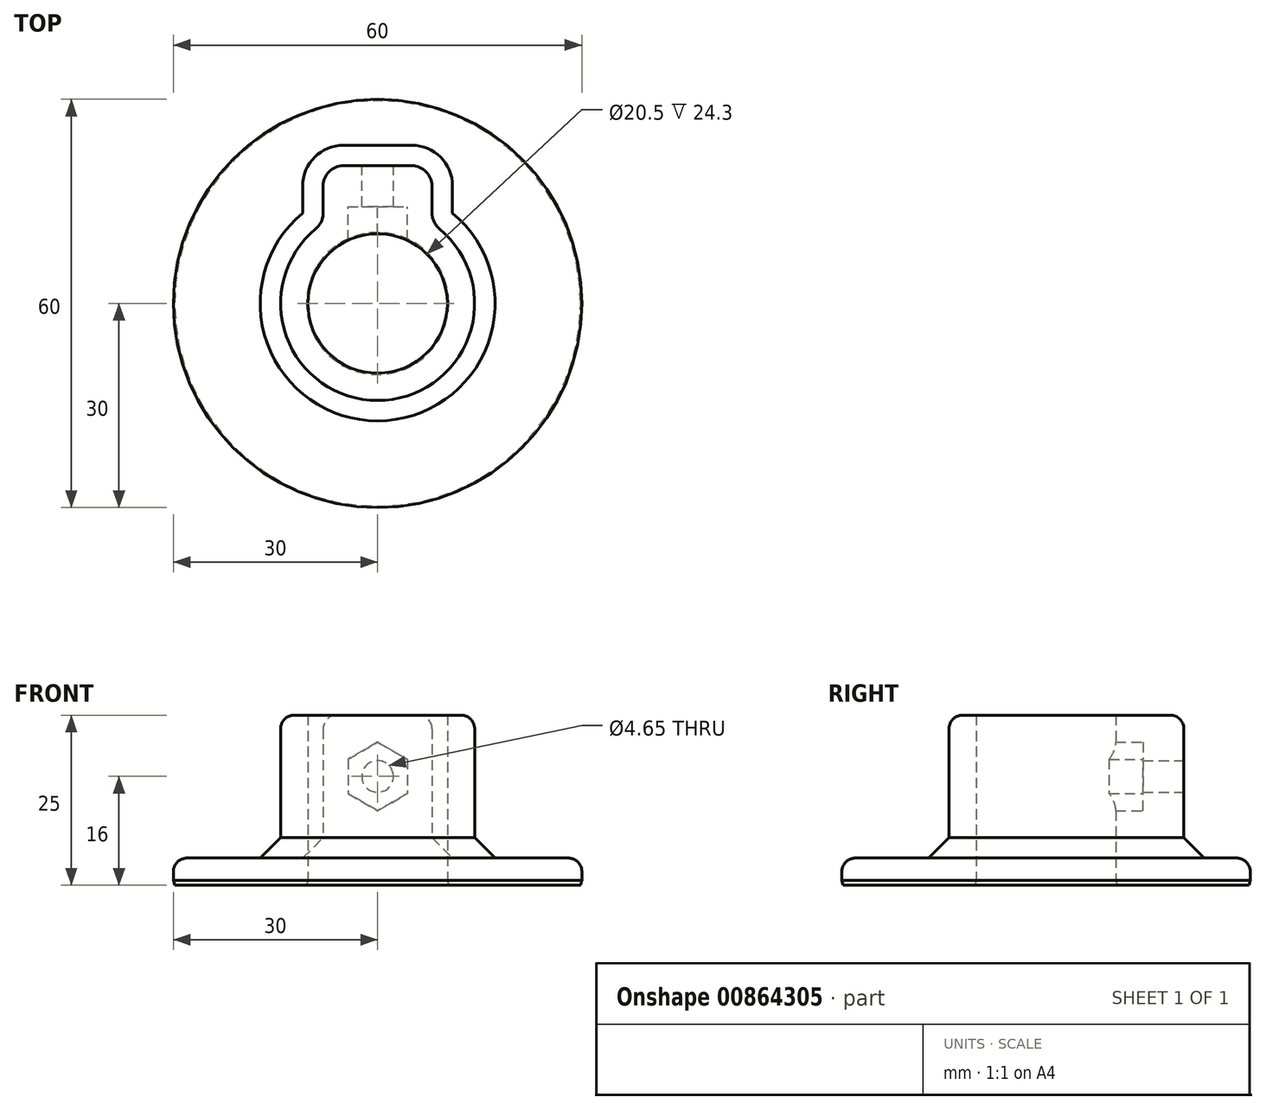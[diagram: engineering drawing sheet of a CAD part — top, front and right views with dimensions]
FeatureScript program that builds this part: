
annotation { "Feature Type Name" : "Feature", "Feature Type Description" : "" }
export const myFeature = defineFeature(function(context is Context, id is Id, definition is map)
    precondition{}
    {
        {
            var Q0;
            Q0=qCreatedBy(makeId("Top.planeOp"),FACE);
            var sketch = newSketch(context, id + "F0", { "sketchPlane" : qUnion([Q0])});
            skCircle(sketch, "E0", {"center": v(0, 0) * mm, "radius": 30 * mm});
            skCircle(sketch, "E1", {"center": v(0, 0) * mm, "radius": 10.25 * mm});
            skCircle(sketch, "E2", {"center": v(0, 0) * mm, "radius": 14.25 * mm});
            skLineSegment(sketch, "E3", {"start": v(-8, 11.8) * mm, "end": v(-8, 20.25) * mm});
            skLineSegment(sketch, "E4", {"start": v(-8, 20.25) * mm, "end": v(8, 20.25) * mm});
            skLineSegment(sketch, "E5", {"start": v(8, 20.25) * mm, "end": v(8, 11.8) * mm});
            skSolve(sketch);
        }
        {
            var Q0;
            Q0=makeQuery(id+"F0.imprint","IMPRINT",FACE,{"disambiguationData":[TD([[makeQuery(id+"F0.imprint","IMPRINT",EDGE,{"derivedFrom":sQuery(id+"F0.wireOp",EDGE,"E0")}),1.0]])]});
            var Q1;
            {var subQ0=sQuery(id+"F0.wireOp",EDGE,"E3");Q1=makeQuery(id+"F0.imprint","IMPRINT",FACE,{"disambiguationData":[TD([[makeQuery(id+"F0.imprint","IMPRINT",EDGE,{"derivedFrom":subQ0}),-1.0]])]});}
            var Q2;
            Q2=makeQuery(id+"F0.imprint","IMPRINT",FACE,{"disambiguationData":[TD([[makeQuery(id+"F0.imprint","IMPRINT",EDGE,{"derivedFrom":sQuery(id+"F0.wireOp",EDGE,"E1")}),-1.0]])]});
            extrude(context, id + "F1", {"entities" : qUnion([Q0, Q1, Q2]), "depth" : 4 * mm, "offsetDistance" : 25 * mm});
        }
        {
            var Q0;
            {var subQ0=sQuery(id+"F0.wireOp",EDGE,"E3");Q0=makeQuery(id+"F0.imprint","IMPRINT",FACE,{"disambiguationData":[TD([[makeQuery(id+"F0.imprint","IMPRINT",EDGE,{"derivedFrom":subQ0}),-1.0]])]});}
            var Q1;
            Q1=makeQuery(id+"F0.imprint","IMPRINT",FACE,{"disambiguationData":[TD([[makeQuery(id+"F0.imprint","IMPRINT",EDGE,{"derivedFrom":sQuery(id+"F0.wireOp",EDGE,"E1")}),-1.0]])]});
            extrude(context, id + "F2", {"entities" : qUnion([Q0, Q1]), "operationType" : NewBodyOperationType.ADD, "depth" : 25 * mm, "offsetDistance" : 25 * mm});
        }
        {
            var Q0;
            Q0=makeQuery(id+"F2.opExtrude","SWEPT_EDGE",EDGE,{"disambiguationData":[OSD([sQuery(id+"F0.wireOp",EDGE,"E2"),sQuery(id+"F0.wireOp",EDGE,"E3")])]});
            var Q1;
            Q1=makeQuery(id+"F2.opExtrude","SWEPT_EDGE",EDGE,{"disambiguationData":[OSD([sQuery(id+"F0.wireOp",EDGE,"E2"),sQuery(id+"F0.wireOp",EDGE,"E5")])]});
            var Q2;
            Q2=makeQuery(id+"F2.opExtrude","SWEPT_EDGE",EDGE,{"disambiguationData":[OSD([sQuery(id+"F0.wireOp",EDGE,"E4"),sQuery(id+"F0.wireOp",EDGE,"E5")])]});
            var Q3;
            Q3=makeQuery(id+"F2.opExtrude","SWEPT_EDGE",EDGE,{"disambiguationData":[OSD([sQuery(id+"F0.wireOp",EDGE,"E3"),sQuery(id+"F0.wireOp",EDGE,"E4")])]});
            fillet(context, id + "F3", {"entities" : qUnion([Q0, Q1, Q2, Q3]), "radius" : 3 * mm, "tangentPropagation" : true, "allowEdgeOverflow" : false});
        }
        {
            var Q0;
            Q0=makeQuery(id+"F2.boolean.opBoolean","INTERSECT",EDGE,{"derivedFrom":[makeQuery(id+"F1.opExtrude","CAP_FACE",FACE,{"disambiguationData":[OSD([sQuery(id+"F0.wireOp",EDGE,"E0"),sQuery(id+"F0.wireOp",EDGE,"E1")])],"isStart":false}),makeQuery(id+"F2.opExtrude","SWEPT_FACE",FACE,{"disambiguationData":[OSD([sQuery(id+"F0.wireOp",EDGE,"E2")])]})]});
            var Q1;
            Q1=makeQuery(id+"F2.boolean.opBoolean","INTERSECT",EDGE,{"derivedFrom":[makeQuery(id+"F1.opExtrude","CAP_FACE",FACE,{"disambiguationData":[OSD([sQuery(id+"F0.wireOp",EDGE,"E0"),sQuery(id+"F0.wireOp",EDGE,"E1")])],"isStart":false}),makeQuery(id+"F2.opExtrude","SWEPT_FACE",FACE,{"disambiguationData":[OSD([sQuery(id+"F0.wireOp",EDGE,"E3")])]})]});
            var Q2;
            Q2=makeQuery(id+"F2.boolean.opBoolean","INTERSECT",EDGE,{"derivedFrom":[makeQuery(id+"F1.opExtrude","CAP_FACE",FACE,{"disambiguationData":[OSD([sQuery(id+"F0.wireOp",EDGE,"E0"),sQuery(id+"F0.wireOp",EDGE,"E1")])],"isStart":false}),makeQuery(id+"F2.opExtrude","SWEPT_FACE",FACE,{"disambiguationData":[OSD([sQuery(id+"F0.wireOp",EDGE,"E5")])]})]});
            chamfer(context, id + "F4", {"entities" : qUnion([Q0, Q1, Q2]), "width" : 3 * mm, "tangentPropagation" : true});
        }
        {
            var Q0;
            Q0=makeQuery(id+"F2.opExtrude","SWEPT_FACE",FACE,{"disambiguationData":[OSD([sQuery(id+"F0.wireOp",EDGE,"E4")])]});
            var sketch = newSketch(context, id + "F5", { "sketchPlane" : qUnion([Q0])});
            skPoint(sketch, "E6", {"position": v(0, 16) * mm});
            skPoint(sketch, "E6.positionSnap0", {"position": v(0, 25) * mm});
            skCircle(sketch, "E7.cCircle", {"center": v(0, 16) * mm, "radius": 4.36 * mm, "construction": true});
            skLineSegment(sketch, "E7.0", {"start": v(-4.36, 13.48) * mm, "end": v(-4.36, 18.52) * mm});
            skLineSegment(sketch, "E7.1", {"start": v(-4.36, 18.52) * mm, "end": v(0, 21.03) * mm});
            skLineSegment(sketch, "E7.2", {"start": v(0, 21.03) * mm, "end": v(4.36, 18.52) * mm});
            skLineSegment(sketch, "E7.3", {"start": v(4.36, 18.52) * mm, "end": v(4.36, 13.48) * mm});
            skLineSegment(sketch, "E7.4", {"start": v(4.36, 13.48) * mm, "end": v(0, 10.97) * mm});
            skLineSegment(sketch, "E7.5", {"start": v(0, 10.97) * mm, "end": v(-4.36, 13.48) * mm});
            skPoint(sketch, "E7.0.midPoint", {"position": v(-4.36, 16) * mm});
            skPoint(sketch, "E8", {"position": v(-5, 16) * mm});
            skSolve(sketch);
        }
        {
            var Q0;
            Q0=makeQuery(id+"F1.opExtrude","CAP_EDGE",EDGE,{"disambiguationData":[OSD([sQuery(id+"F0.wireOp",EDGE,"E1")])],"isStart":true});
            var Q1;
            Q1=makeQuery(id+"F1.opExtrude","CAP_EDGE",EDGE,{"disambiguationData":[OSD([sQuery(id+"F0.wireOp",EDGE,"E0")])],"isStart":true});
            chamfer(context, id + "F6", {"entities" : qUnion([Q0, Q1]), "chamferType" : ChamferType.TWO_OFFSETS, "width1" : .2 * mm, "oppositeDirection" : false, "width2" : .7 * mm, "tangentPropagation" : true});
        }
        {
            var Q0;
            Q0=makeQuery(id+"F5.imprint","IMPRINT",FACE,{"disambiguationData":[TD([[makeQuery(id+"F5.imprint","IMPRINT",EDGE,{"derivedFrom":sQuery(id+"F5.wireOp",EDGE,"E7.0")}),-1.0]])]});
            extrude(context, id + "F7", {"entities" : qUnion([Q0]), "operationType" : NewBodyOperationType.REMOVE, "oppositeDirection" : true, "depth" : 25 * mm, "offsetDistance" : 25 * mm, "hasSecondDirection" : true, "secondDirectionOppositeDirection" : true, "secondDirectionDepth" : 6 * mm});
        }
        {
            var Q0;
            Q0=sQuery(id+"F5.wireOp",VERTEX,"E6");
            var Q1;
            Q1=makeQuery(id+"F1.opExtrude","SWEPT_BODY",BODY,{"disambiguationData":[OSD([sQuery(id+"F0.wireOp",EDGE,"E0"),sQuery(id+"F0.wireOp",EDGE,"E1")])]});
            hole(context, id + "F8", {"style" : HoleStyle.SIMPLE, "endStyle" : HoleEndStyle.BLIND, "holeDiameter" : 4.65 * mm, "majorDiameter" : 5 * mm, "holeDepth" : 8 * mm, "isTappedThrough" : true, "tappedDepth" : 12 * mm, "tapClearance" : 3, "locations" : qUnion([Q0]), "scope" : qUnion([Q1])});
        }
        {
            var Q0;
            Q0=makeQuery(id+"F1.opExtrude","CAP_EDGE",EDGE,{"disambiguationData":[OSD([sQuery(id+"F0.wireOp",EDGE,"E0")])],"isStart":false});
            var Q1;
            Q1=makeQuery(id+"F2.opExtrude","CAP_EDGE",EDGE,{"disambiguationData":[OSD([sQuery(id+"F0.wireOp",EDGE,"E2")])],"isStart":false});
            fillet(context, id + "F9", {"entities" : qUnion([Q0, Q1]), "radius" : 2 * mm, "tangentPropagation" : true, "allowEdgeOverflow" : false});
        }
    });
